# Revit family: portal_deceuninck_shema-g3
name_source: partatom
category: Двери
revit_build: Autodesk Revit 2016 (Build: 20150714_1515(x64)
units: mm (PartAtom-declared; Revit-internal decimal feet)

## family parameters
Всегда вертикально = Да
Заголовок OmniClass = Windows
Номер OmniClass = 23.30.20.00
Общий = Нет
Основа = Стена
При загрузке вырезать с полостями = Нет
Точка расчета площади = Нет

## types (1)
- Портал HST 76 - схема C
    Rед = 1.0000 (м²·K)/Вт
    Rпрофиля = 0.7700 (м²·K)/Вт
    Rстеклопакета = 0.7600 (м²·K)/Вт
    λ краевой зоны стеклопакета = 0.0600 (м²·K)/Вт
    Аналитическая конструкция = <Нет>
    Артикул рамы/армирование рамы = HS 176 / NA 57
    Артикул створки/армирование рстворки = HS 4761D  / NA 66
    Высота = 0 мм
    ГОСТ = RAL-GZ 716/1
    Замыкание стены = По основе
    Материал-Рама = <По категории>
    Материал-Стеклопакет = <По категории>
    Монтажный зазор.Боковой = 20 мм
    Наименование = Портал HST 76 Схема G3
    Огнестойкость = Е-30
    Примерная высота = 0 мм
    Примерная ширина = 0 мм
    Профильная система = HST 76
    Толщина = 0 мм
    Толщина стеклопакета = 48
    Ширина = 0 мм
    Ширина профиля = 76 мм

## geometry (parser evidence)
native form markers: Blend x30
no freeform markers — native parametric forms only
